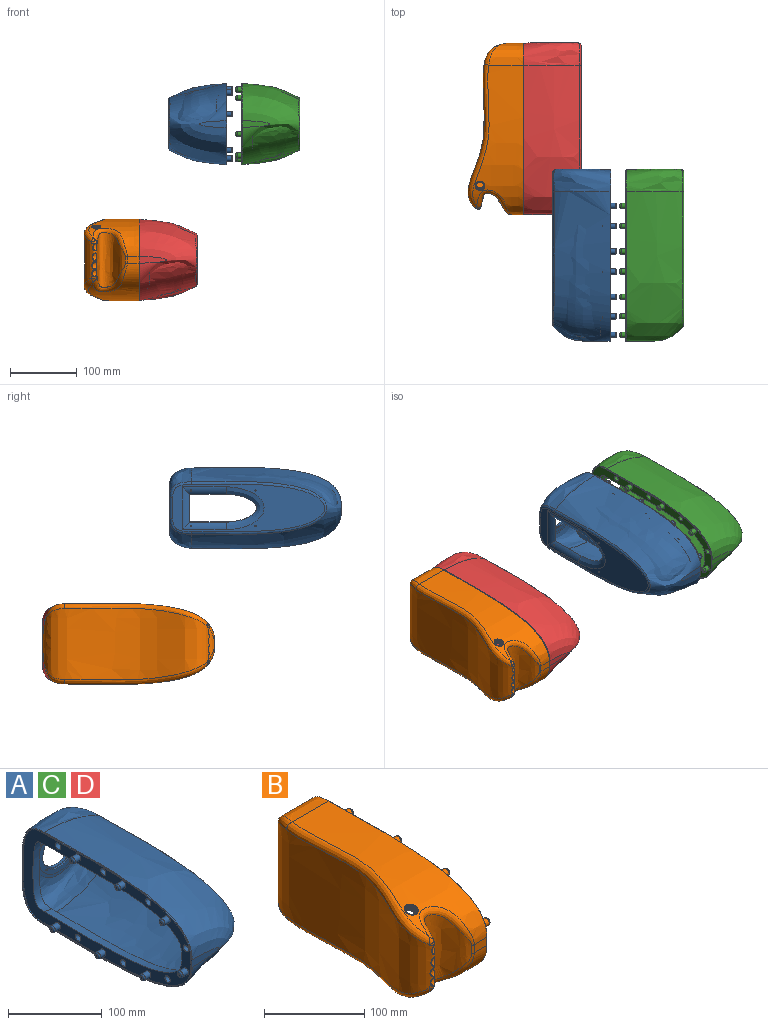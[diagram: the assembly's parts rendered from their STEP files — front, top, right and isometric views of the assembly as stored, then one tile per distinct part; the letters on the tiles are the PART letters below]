
ASSEMBLY  parts=4 mates=1
PART A: 85 faces, bbox 235.2x294.7x145.9 mm
  f0: plane 256.02x120.86mm, normal (-1,0,0), area 8418.6mm2, adj f38,f39,f40,f41,f42,f44,f46,f48
  f1: plane 49x49mm, normal (0,-1,0), area 223.8mm2, adj f2,f3
  f2: cylinder r=23mm len=46mm, axis (0,-1,0), area 505.8mm2, adj f1,f4
  f3: cylinder r=24.5mm len=49mm, axis (0,-1,0), area 230.9mm2, adj f1,f5
  f4: plane 61x61mm, normal (0,1,0), area 1248mm2, adj f2,f6,f30,f31,f32,f33
  f5: plane 61x61mm, normal (0,-1,0), area 1024.2mm2, adj f3,f8,f30,f31,f32,f33
  f6: cylinder r=30.5mm len=61mm, axis (0,1,0), area 191.6mm2, adj f4,f20
  f7: cylinder r=5mm len=32.5mm, axis (0,0,-1), area 255.2mm2, adj f18,f19,f20,f21
  f8: cylinder r=30.5mm len=61mm, axis (0,-1,0), area 191.6mm2, adj f5,f13
  f9: cylinder r=1mm len=5mm, axis (1,0,0), area 31.4mm2, adj f14,f18
  f10: cylinder r=1mm len=4.25mm, axis (1,0,0), area 24.1mm2, adj f14,f28
  f11: cylinder r=1mm len=4.25mm, axis (1,0,0), area 24.1mm2, adj f14,f27
  f12: cylinder r=1mm len=5mm, axis (1,0,0), area 31.4mm2, adj f14,f18
  f13: plane 70x66mm, normal (0,-1,0), area 838.2mm2, adj f8,f14,f17
  f14: plane 233.9x77.75mm, normal (-1,0,0), area 10556.5mm2, adj f9,f10,f11,f12,f13,f16,f17,f26
  f15: plane 25.42x9.32mm, normal (0,1,0), area 171.6mm2, adj f16,f35
  f16: bspline ~219x110.67mm, area 32952.3mm2, adj f14,f15,f17,f34,f35,f36,f37
  f17: bspline ~204.64x110mm, area 5721.8mm2, adj f13,f14,f16,f36,f37
  f18: plane 227.73x71.58mm, normal (1,0,0), area 7233.4mm2, adj f7,f9,f12,f19,f21,f22,f26,f27
  f19: bspline ~37.57x23.06mm, area 226.7mm2, adj f7,f18,f22,f25
  f20: plane 70x66.02mm, normal (0,1,0), area 838.2mm2, adj f6,f7,f25
  f21: bspline ~33.5x22.97mm, area 226.7mm2, adj f7,f18,f22,f25
  f22: bspline ~248.96x80.08mm, area 2059.5mm2, adj f18,f19,f21,f24
  f23: plane 65.08x34.08mm, normal (0,-1,0), area 324.2mm2, adj f24,f77,f78,f79
  f24: offset ~229x169.47mm, area 52271.3mm2, adj f22,f23,f25,f78,f79
  f25: offset ~214.64x120mm, area 9931.3mm2, adj f19,f20,f21,f24,f80
  f26: bspline ~64.4x57.74mm, area 1562.2mm2, adj f14,f18,f27,f28
  f27: cylinder r=15mm len=65.71mm, axis (0,-1,0), area 757.5mm2, adj f11,f14,f18,f26,f29
  f28: cylinder r=15mm len=65.73mm, axis (0,-1,0), area 757.6mm2, adj f10,f14,f18,f26,f29
  f29: cylinder r=15mm len=64.36mm, axis (0,0,1), area 670.9mm2, adj f14,f18,f27,f28
  f30: cylinder r=1mm len=5mm, axis (0,-1,0), area 31.4mm2, adj f4,f5
  f31: cylinder r=1mm len=5mm, axis (0,-1,0), area 31.4mm2, adj f4,f5
  f32: cylinder r=1mm len=5mm, axis (0,-1,0), area 31.4mm2, adj f4,f5
  f33: cylinder r=1mm len=5mm, axis (0,-1,0), area 31.4mm2, adj f4,f5
  f34: bspline ~221.19x53.32mm, area 2075.3mm2, adj f16,f35,f36,f39
  f35: plane 10.12x8.9mm, normal (0.94,0.33,0), area 94.4mm2, adj f15,f16,f34,f37,f40
  f36: bspline ~114.45x30.34mm, area 1363.5mm2, adj f16,f17,f34,f37,f38
  f37: bspline ~219.18x50.81mm, area 2075.2mm2, adj f16,f17,f35,f36,f41
  f38: bspline ~92.2x19.24mm, area 1291.4mm2, adj f0,f36,f39,f41
  f39: bspline ~209.92x42.23mm, area 2620.1mm2, adj f0,f34,f38,f40
  f40: plane 11.45x10.03mm, normal (0.17,0.99,0), area 116.2mm2, adj f0,f35,f39,f41
  f41: bspline ~210.31x41.79mm, area 2620mm2, adj f0,f37,f38,f40
  f42: cylinder r=4mm len=11mm, axis (-1,0,0), area 276.5mm2, adj f0,f43
  f43: plane 8x8mm, normal (-1,0,0), area 50.3mm2, adj f42
  f44: cylinder r=4mm len=11mm, axis (-1,0,0), area 276.5mm2, adj f0,f45
  f45: plane 8x8mm, normal (-1,0,0), area 50.3mm2, adj f44
  f46: cylinder r=4mm len=11mm, axis (-1,0,0), area 276.5mm2, adj f0,f47
  f47: plane 8x8mm, normal (-1,0,0), area 50.3mm2, adj f46
  f48: cylinder r=4mm len=11mm, axis (-1,0,0), area 276.5mm2, adj f0,f49
  f49: plane 8x8mm, normal (-1,0,0), area 50.3mm2, adj f48
  f50: cylinder r=4mm len=11mm, axis (-1,0,0), area 276.5mm2, adj f0,f51
  f51: plane 8x8mm, normal (-1,0,0), area 50.3mm2, adj f50
  f52: cylinder r=4mm len=11mm, axis (-1,0,0), area 276.5mm2, adj f0,f53
  f53: plane 8x8mm, normal (-1,0,0), area 50.3mm2, adj f52
  f54: cylinder r=4mm len=11mm, axis (-1,0,0), area 276.5mm2, adj f0,f55
  f55: plane 8x8mm, normal (-1,0,0), area 50.3mm2, adj f54
  f56: cylinder r=4mm len=8mm, axis (1,0,0), area 201.1mm2, adj f0,f58
  f57: plane 4x4mm, normal (-1,0,0), area 12.6mm2, adj f58
  f58: torus R=2mm, axis (-1,0,0), area 64.6mm2, adj f56,f57
  f59: cylinder r=4mm len=8mm, axis (1,0,0), area 201.1mm2, adj f0,f61
  f60: plane 4x4mm, normal (-1,0,0), area 12.6mm2, adj f61
  f61: torus R=2mm, axis (-1,0,0), area 64.6mm2, adj f59,f60
  f62: cylinder r=4mm len=8mm, axis (1,0,0), area 201.1mm2, adj f0,f64
  f63: plane 4x4mm, normal (-1,0,0), area 12.6mm2, adj f64
  f64: torus R=2mm, axis (-1,0,0), area 64.6mm2, adj f62,f63
  f65: cylinder r=4mm len=8mm, axis (1,0,0), area 201.1mm2, adj f0,f67
  f66: plane 4x4mm, normal (-1,0,0), area 12.6mm2, adj f67
  f67: torus R=2mm, axis (-1,0,0), area 64.6mm2, adj f65,f66
  f68: cylinder r=4mm len=8mm, axis (1,0,0), area 201.1mm2, adj f0,f70
  f69: plane 4x4mm, normal (-1,0,0), area 12.6mm2, adj f70
  f70: torus R=2mm, axis (-1,0,0), area 64.6mm2, adj f68,f69
  f71: cylinder r=4mm len=8mm, axis (1,0,0), area 201.1mm2, adj f0,f73
  f72: plane 4x4mm, normal (-1,0,0), area 12.6mm2, adj f73
  f73: torus R=2mm, axis (-1,0,0), area 64.6mm2, adj f71,f72
  f74: cylinder r=4mm len=8mm, axis (1,0,0), area 201.1mm2, adj f0,f76
  f75: plane 4x4mm, normal (-1,0,0), area 12.6mm2, adj f76
  f76: torus R=2mm, axis (-1,0,0), area 64.6mm2, adj f74,f75
  f77: plane 257.05x121.92mm, normal (-1,0,0), area 660.2mm2, adj f23,f78,f79,f80,f81,f82,f83,f84
  f78: extruded ~224x55.88mm, area 249mm2, adj f23,f24,f77,f80
  f79: extruded ~224x55.88mm, area 248.9mm2, adj f23,f24,f77,f80
  f80: extruded ~120x32.93mm, area 159.6mm2, adj f25,f77,f78,f79
  f81: extruded ~223x54.88mm, area 247.4mm2, adj f0,f77,f82,f84
  f82: plane 10x1mm, normal (0,1,0), area 10mm2, adj f0,f77,f81,f83
  f83: extruded ~223x54.88mm, area 247.3mm2, adj f0,f77,f82,f84
  f84: extruded ~118x31.93mm, area 154.2mm2, adj f0,f77,f81,f83
PART B: 129 faces, bbox 103.6x282.6x131.8 mm
  f0: plane 256.12x120.97mm, normal (1,0,0), area 7983.5mm2, adj f12,f15,f18,f21,f24,f27,f30,f33
  f1: plane 28.67x27.53mm, normal (-0.01,0.33,-0.94), area 487.9mm2, adj f90,f91,f93,f94,f95,f96,f99,f101
  f2: plane 14.06x13.27mm, normal (0.01,-0.33,0.94), area 43.6mm2, adj f92,f93,f94,f95,f96
  f3: extruded ~224x75.53mm, area 12312.4mm2, adj f41,f42,f46,f47,f97,f114
  f4: bspline ~38.52x35.85mm, area 144.7mm2, adj f6,f11,f65,f107
  f5: bspline ~19.02x15.19mm, area 57mm2, adj f6,f9,f10,f62,f102
  f6: extruded ~82.3x49.16mm, area 5374.4mm2, adj f4,f5,f7,f61,f63,f65,f104,f106
  f7: extruded ~238.19x107.76mm, area 25111.6mm2, adj f6,f8,f9,f61,f62,f64,f66,f67
  f8: bspline ~166.2x20.05mm, area 532.7mm2, adj f7,f11,f66,f101,f103
  f9: bspline ~25.78x16.55mm, area 71mm2, adj f5,f7,f10,f62,f98
  f10: extruded ~17.83x10.99mm, area 84.5mm2, adj f5,f9,f100
  f11: extruded ~219x53.14mm, area 7793mm2, adj f4,f8,f69,f70,f105,f110
  f12: cylinder r=4mm len=8mm, axis (-1,0,0), area 201.1mm2, adj f0,f14
  f13: plane 4x4mm, normal (1,0,0), area 12.6mm2, adj f14
  f14: torus R=2mm, axis (-1,0,0), area 64.6mm2, adj f12,f13
  f15: cylinder r=4mm len=8mm, axis (-1,0,0), area 201.1mm2, adj f0,f17
  f16: plane 4x4mm, normal (1,0,0), area 12.6mm2, adj f17
  f17: torus R=2mm, axis (-1,0,0), area 64.6mm2, adj f15,f16
  f18: cylinder r=4mm len=8mm, axis (-1,0,0), area 201.1mm2, adj f0,f20
  f19: plane 4x4mm, normal (1,0,0), area 12.6mm2, adj f20
  f20: torus R=2mm, axis (-1,0,0), area 64.6mm2, adj f18,f19
  f21: cylinder r=4mm len=8mm, axis (-1,0,0), area 201.1mm2, adj f0,f23
  f22: plane 4x4mm, normal (1,0,0), area 12.6mm2, adj f23
  f23: torus R=2mm, axis (-1,0,0), area 64.6mm2, adj f21,f22
  f24: cylinder r=4mm len=8mm, axis (-1,0,0), area 201.1mm2, adj f0,f26
  f25: plane 4x4mm, normal (1,0,0), area 12.6mm2, adj f26
  f26: torus R=2mm, axis (-1,0,0), area 64.6mm2, adj f24,f25
  f27: cylinder r=4mm len=8mm, axis (-1,0,0), area 201.1mm2, adj f0,f29
  f28: plane 4x4mm, normal (1,0,0), area 12.6mm2, adj f29
  f29: torus R=2mm, axis (-1,0,0), area 64.6mm2, adj f27,f28
  f30: cylinder r=4mm len=8mm, axis (-1,0,0), area 201.1mm2, adj f0,f32
  f31: plane 4x4mm, normal (1,0,0), area 12.6mm2, adj f32
  f32: torus R=2mm, axis (-1,0,0), area 64.6mm2, adj f30,f31
  f33: cylinder r=4mm len=8mm, axis (-1,0,0), area 201.1mm2, adj f0,f35
  f34: plane 4x4mm, normal (1,0,0), area 12.6mm2, adj f35
  f35: torus R=2mm, axis (-1,0,0), area 64.6mm2, adj f33,f34
  f36: cylinder r=4mm len=8mm, axis (-1,0,0), area 201.1mm2, adj f0,f38
  f37: plane 4x4mm, normal (1,0,0), area 12.6mm2, adj f38
  f38: torus R=2mm, axis (-1,0,0), area 64.6mm2, adj f36,f37
  f39: extruded ~256.27x107.76mm, area 30806.9mm2, adj f44,f46,f47,f48,f49,f50,f51,f52
  f40: extruded ~224x69.32mm, area 12836mm2, adj f41,f43,f51,f54,f114
  f41: plane 17.97x10mm, normal (0,-1,0), area 179.6mm2, adj f3,f40,f48,f114
  f42: extruded ~60x51.41mm, area 2938.4mm2, adj f3,f43,f49,f114
  f43: extruded ~60x51.41mm, area 2892.6mm2, adj f40,f42,f52,f114
  f44: bspline ~8.26x4.65mm, area 30mm2, adj f39,f45,f46,f124
  f45: bspline ~7.23x6.82mm, area 25.1mm2, adj f44,f46,f47
  f46: bspline ~52.01x43.21mm, area 842.1mm2, adj f3,f39,f44,f45,f48
  f47: bspline ~217.81x34.47mm, area 2456.3mm2, adj f3,f39,f45,f49
  f48: cylinder r=7mm len=10mm, axis (0,0,-1), area 29.6mm2, adj f39,f41,f46,f51
  f49: bspline ~82.22x35.79mm, area 404.7mm2, adj f39,f42,f47,f52
  f50: bspline ~8.3x4.65mm, area 30mm2, adj f39,f51,f53,f128
  f51: bspline ~99.19x52mm, area 839.5mm2, adj f39,f40,f48,f50,f53
  f52: bspline ~84.32x35.8mm, area 404.5mm2, adj f39,f43,f49,f54
  f53: bspline ~7.22x6.78mm, area 19.8mm2, adj f50,f51,f54
  f54: bspline ~218.29x34.33mm, area 2456.2mm2, adj f39,f40,f52,f53
  f55: bspline ~44.88x17.4mm, area 881.7mm2, adj f0,f56,f59,f60
  f56: bspline ~44.47x17.8mm, area 880.8mm2, adj f0,f55,f57,f60
  f57: bspline ~208.47x40.79mm, area 3617.4mm2, adj f0,f56,f58,f60
  f58: plane 16.09x10mm, normal (0,1,0), area 160.9mm2, adj f0,f57,f59,f60
  f59: bspline ~208.88x40.36mm, area 3617.3mm2, adj f0,f55,f58,f60
  f60: plane 247.12x111.96mm, normal (-1,0,0), area 5900mm2, adj f55,f56,f57,f58,f59,f109,f110,f111
  f61: offset ~12.4x11.3mm, area 0.2mm2, adj f6,f7,f63
  f62: offset ~13.7x11.82mm, area 0.2mm2, adj f5,f7,f9
  f63: bspline ~94.51x52mm, area 246.8mm2, adj f6,f61,f64,f65,f71
  f64: bspline ~214.27x29.33mm, area 687.8mm2, adj f7,f63,f67,f71
  f65: cylinder r=2mm len=10mm, axis (0,0,-1), area 8.5mm2, adj f4,f6,f63,f70
  f66: bspline ~77.21x32.96mm, area 101.6mm2, adj f7,f8,f67,f69
  f67: bspline ~79.31x33.01mm, area 101.6mm2, adj f7,f64,f66,f68
  f68: extruded ~55x35.82mm, area 1414mm2, adj f67,f69,f71,f111
  f69: extruded ~55x35.82mm, area 1436.5mm2, adj f11,f66,f68,f109
  f70: plane 10x2.38mm, normal (0,1,0), area 23.8mm2, adj f11,f65,f71,f112
  f71: extruded ~219x59.94mm, area 8441mm2, adj f63,f64,f68,f70,f113
  f72: cylinder r=4mm len=11mm, axis (1,0,0), area 276.5mm2, adj f0,f73
  f73: plane 8x8mm, normal (1,0,0), area 50.3mm2, adj f72
  f74: cylinder r=4mm len=11mm, axis (1,0,0), area 276.5mm2, adj f0,f75
  f75: plane 8x8mm, normal (1,0,0), area 50.3mm2, adj f74
  f76: cylinder r=4mm len=11mm, axis (1,0,0), area 276.5mm2, adj f0,f77
  f77: plane 8x8mm, normal (1,0,0), area 50.3mm2, adj f76
  f78: cylinder r=4mm len=11mm, axis (1,0,0), area 276.5mm2, adj f0,f79
  f79: plane 8x8mm, normal (1,0,0), area 50.3mm2, adj f78
  f80: cylinder r=4mm len=11mm, axis (1,0,0), area 276.5mm2, adj f0,f81
  f81: plane 8x8mm, normal (1,0,0), area 50.3mm2, adj f80
  f82: cylinder r=4mm len=11mm, axis (1,0,0), area 276.5mm2, adj f0,f83
  f83: plane 8x8mm, normal (1,0,0), area 50.3mm2, adj f82
  f84: cylinder r=4mm len=11mm, axis (1,0,0), area 276.5mm2, adj f0,f85
  f85: plane 8x8mm, normal (1,0,0), area 50.3mm2, adj f84
  f86: cylinder r=4mm len=11mm, axis (1,0,0), area 276.5mm2, adj f0,f87
  f87: plane 8x8mm, normal (1,0,0), area 50.3mm2, adj f86
  f88: cylinder r=4mm len=11mm, axis (1,0,0), area 276.5mm2, adj f0,f89
  f89: plane 8x8mm, normal (1,0,0), area 50.3mm2, adj f88
  f90: cylinder r=15mm len=22.55mm, axis (0.01,-0.33,0.94), area 72.8mm2, adj f1,f103,f105,f107,f108
  f91: cylinder r=15mm len=11.93mm, axis (0.01,-0.33,0.94), area 28.5mm2, adj f1,f98,f99,f100,f102,f104
  f92: cylinder r=6.9mm len=13.81mm, axis (0.01,-0.33,0.94), area 26.4mm2, adj f2,f97
  f93: bspline ~13.99x13.76mm, area 161.7mm2, adj f1,f2,f95,f96
  f94: bspline ~13.98x13.54mm, area 161.2mm2, adj f1,f2,f95,f96
  f95: bspline ~14.06x13.62mm, area 38.8mm2, adj f1,f2,f93,f94
  f96: cylinder r=5.62mm len=12.96mm, axis (-0.01,0.33,-0.94), area 57.1mm2, adj f1,f2,f93,f94
  f97: bspline ~14.42x13.77mm, area 21.1mm2, adj f3,f92
  f98: bspline ~3.83x2.69mm, area 3.6mm2, adj f9,f91,f99,f100
  f99: bspline ~12.12x4.78mm, area 1.2mm2, adj f1,f7,f91,f98,f101
  f100: bspline ~12.15x5.86mm, area 8.5mm2, adj f10,f91,f98,f102
  f101: bspline ~30.63x11.16mm, area 20.3mm2, adj f1,f7,f8,f99,f103
  f102: bspline ~2.77x2.28mm, area 2.4mm2, adj f5,f91,f100,f104
  f103: bspline ~3.37x2.93mm, area 3.3mm2, adj f1,f8,f90,f101,f105
  f104: bspline ~7.44x3.18mm, area 1mm2, adj f1,f6,f91,f102,f106
  f105: bspline ~22.61x21.37mm, area 28.1mm2, adj f11,f90,f103,f107
  f106: bspline ~15.38x7.72mm, area 9.6mm2, adj f1,f6,f104,f108
  f107: bspline ~2.4x1.91mm, area 2mm2, adj f4,f90,f105,f108
  f108: bspline ~8.89x2.47mm, area 2.1mm2, adj f1,f6,f90,f106,f107
  f109: bspline ~60.68x49.99mm, area 55.6mm2, adj f60,f69,f110,f111
  f110: bspline ~267.57x92.17mm, area 189.1mm2, adj f11,f60,f109,f112
  f111: bspline ~69.71x50.22mm, area 55.6mm2, adj f60,f68,f109,f113
  f112: cylinder r=0.5mm len=10mm, axis (0,0,1), area 7.9mm2, adj f60,f70,f110,f113
  f113: bspline ~267.53x92.02mm, area 189.1mm2, adj f60,f71,f111,f112
  f114: plane 258.34x123.21mm, normal (1,0,0), area 540mm2, adj f3,f40,f41,f42,f43,f115,f116,f117
  f115: extruded ~223x54.88mm, area 247.4mm2, adj f0,f114,f116,f118
  f116: plane 10x1mm, normal (0,-1,0), area 10mm2, adj f0,f114,f115,f117
  f117: extruded ~223x54.88mm, area 247.3mm2, adj f0,f114,f116,f118
  f118: extruded ~118x31.93mm, area 154.2mm2, adj f0,f114,f115,f117
  f119: bspline ~23.96x16.05mm, area 51.4mm2, adj f127,f128
  f120: bspline ~17.9x14.29mm, area 59mm2, adj f126
  f121: bspline ~19.25x15.84mm, area 51.6mm2, adj f125
  f122: bspline ~18.93x17.94mm, area 52.1mm2, adj f123,f124
  f123: bspline ~11.73x6.32mm, area 20mm2, adj f39,f122,f124
  f124: bspline ~1.31x1.1mm, area 0.8mm2, adj f44,f122,f123
  f125: bspline ~11.75x6.79mm, area 22.5mm2, adj f39,f121
  f126: bspline ~11.92x7.69mm, area 26.4mm2, adj f39,f120
  f127: bspline ~10.85x7.48mm, area 23.1mm2, adj f39,f119,f128
  f128: bspline ~2.41x0.98mm, area 1.8mm2, adj f50,f119,f127
PART C: same geometry as A
PART D: same geometry as A
PLACE A rot(axis=(0,1,0),180deg) t=(-205.46,-5.02,-22.73)mm
PLACE B t=(-162.79,185.04,-226.45)mm
PLACE C t=(-8.66,-5.02,-22.73)mm
PLACE D t=(-162.79,185.04,-226.45)mm
MATE fastened D.f44 <-> B.f18  axis (-1,0,0) through (-248.79,49.7,-265.77)mm
